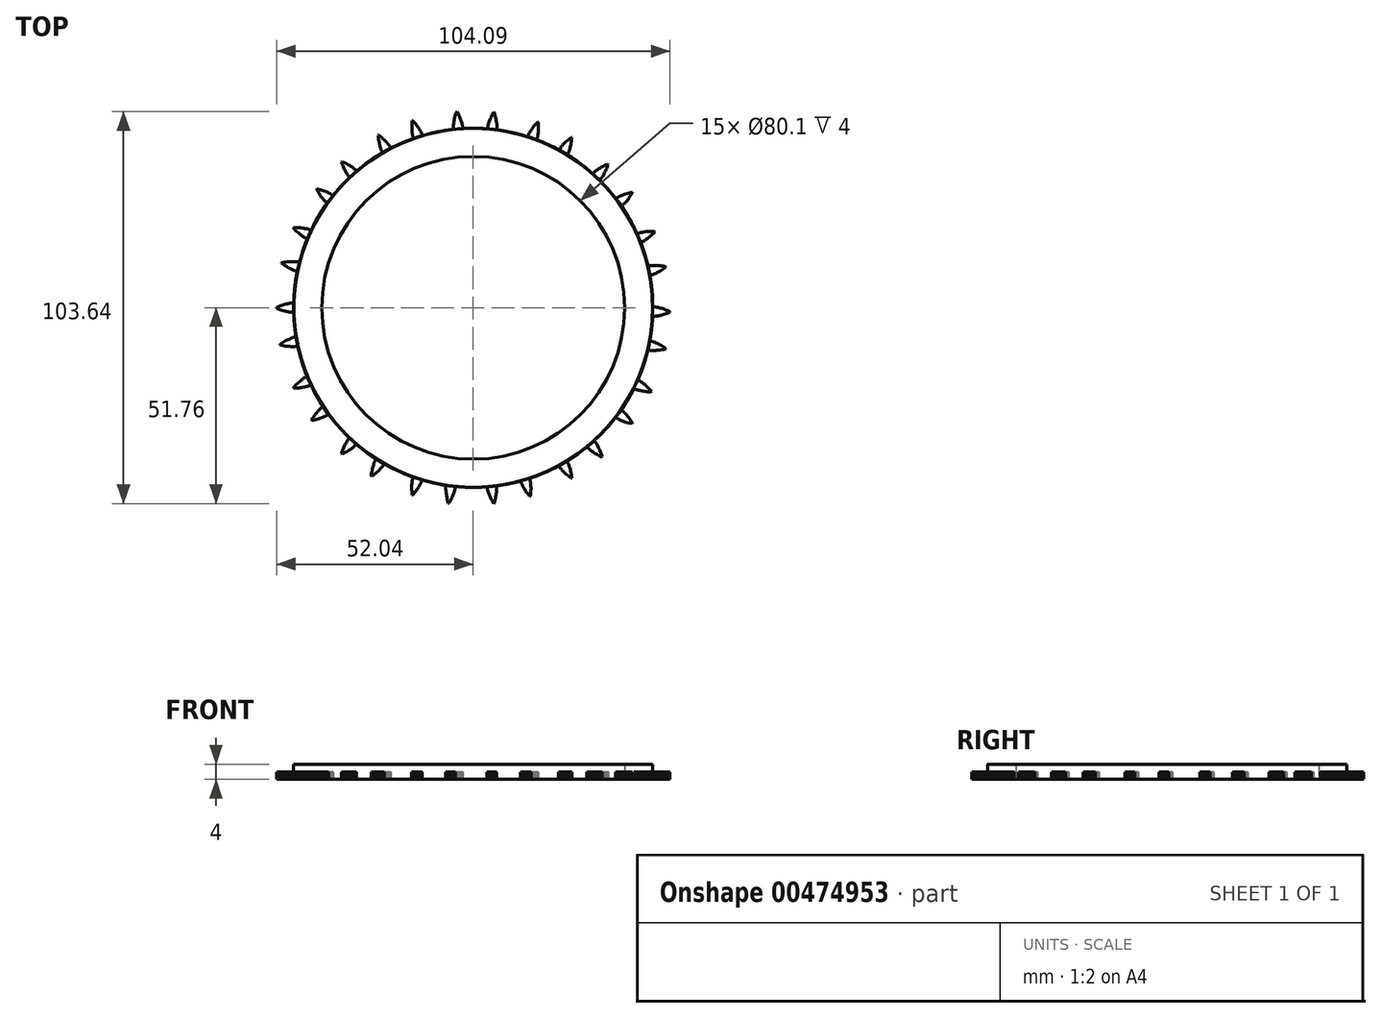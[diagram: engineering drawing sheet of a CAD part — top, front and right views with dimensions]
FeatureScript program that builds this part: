
annotation { "Feature Type Name" : "Feature", "Feature Type Description" : "" }
export const myFeature = defineFeature(function(context is Context, id is Id, definition is map)
    precondition{}
    {
        {
            var Q0;
            Q0=qCreatedBy(makeId("Top.planeOp"),FACE);
            var sketch = newSketch(context, id + "F0", { "sketchPlane" : qUnion([Q0])});
            skLineSegment(sketch, "E0", {"start": v(-4.56, -46.57) * mm, "end": v(-4.74, -47.51) * mm});
            skLineSegment(sketch, "E1", {"start": v(-4.74, -47.51) * mm, "end": v(-4.74, -47.52) * mm});
            skLineSegment(sketch, "E2", {"start": v(-4.74, -47.52) * mm, "end": v(-4.75, -47.57) * mm});
            skLineSegment(sketch, "E3", {"start": v(-4.75, -47.57) * mm, "end": v(-4.76, -47.64) * mm});
            skLineSegment(sketch, "E4", {"start": v(-4.76, -47.64) * mm, "end": v(-4.78, -47.75) * mm});
            skLineSegment(sketch, "E5", {"start": v(-4.78, -47.75) * mm, "end": v(-4.81, -47.89) * mm});
            skLineSegment(sketch, "E6", {"start": v(-4.81, -47.89) * mm, "end": v(-4.85, -48.05) * mm});
            skLineSegment(sketch, "E7", {"start": v(-4.85, -48.05) * mm, "end": v(-4.9, -48.25) * mm});
            skLineSegment(sketch, "E8", {"start": v(-4.9, -48.25) * mm, "end": v(-4.97, -48.47) * mm});
            skLineSegment(sketch, "E9", {"start": v(-4.97, -48.47) * mm, "end": v(-5.06, -48.72) * mm});
            skLineSegment(sketch, "E10", {"start": v(-5.06, -48.72) * mm, "end": v(-5.15, -49) * mm});
            skLineSegment(sketch, "E11", {"start": v(-5.15, -49) * mm, "end": v(-5.27, -49.31) * mm});
            skLineSegment(sketch, "E12", {"start": v(-5.27, -49.31) * mm, "end": v(-5.41, -49.64) * mm});
            skLineSegment(sketch, "E13", {"start": v(-5.41, -49.64) * mm, "end": v(-5.57, -50) * mm});
            skLineSegment(sketch, "E14", {"start": v(-5.57, -50) * mm, "end": v(-5.75, -50.38) * mm});
            skLineSegment(sketch, "E15", {"start": v(-5.75, -50.38) * mm, "end": v(-5.96, -50.79) * mm});
            skLineSegment(sketch, "E16", {"start": v(-5.96, -50.79) * mm, "end": v(-6.19, -51.21) * mm});
            skLineSegment(sketch, "E17", {"start": v(-6.19, -51.21) * mm, "end": v(-6.44, -51.66) * mm});
            skLineSegment(sketch, "E18", {"start": v(-6.6, -51.64) * mm, "end": v(-6.74, -51.14) * mm});
            skLineSegment(sketch, "E19", {"start": v(-6.74, -51.14) * mm, "end": v(-6.86, -50.67) * mm});
            skLineSegment(sketch, "E20", {"start": v(-6.86, -50.67) * mm, "end": v(-6.96, -50.23) * mm});
            skLineSegment(sketch, "E21", {"start": v(-6.96, -50.23) * mm, "end": v(-7.04, -49.81) * mm});
            skLineSegment(sketch, "E22", {"start": v(-7.04, -49.81) * mm, "end": v(-7.1, -49.43) * mm});
            skLineSegment(sketch, "E23", {"start": v(-7.1, -49.43) * mm, "end": v(-7.16, -49.07) * mm});
            skLineSegment(sketch, "E24", {"start": v(-7.16, -49.07) * mm, "end": v(-7.2, -48.75) * mm});
            skLineSegment(sketch, "E25", {"start": v(-7.2, -48.75) * mm, "end": v(-7.22, -48.45) * mm});
            skLineSegment(sketch, "E26", {"start": v(-7.22, -48.45) * mm, "end": v(-7.24, -48.19) * mm});
            skLineSegment(sketch, "E27", {"start": v(-7.24, -48.19) * mm, "end": v(-7.25, -47.95) * mm});
            skLineSegment(sketch, "E28", {"start": v(-7.25, -47.95) * mm, "end": v(-7.25, -47.75) * mm});
            skLineSegment(sketch, "E29", {"start": v(-7.25, -47.75) * mm, "end": v(-7.25, -47.58) * mm});
            skLineSegment(sketch, "E30", {"start": v(-7.25, -47.58) * mm, "end": v(-7.24, -47.44) * mm});
            skLineSegment(sketch, "E31", {"start": v(-7.24, -47.44) * mm, "end": v(-7.24, -47.33) * mm});
            skLineSegment(sketch, "E32", {"start": v(-7.24, -47.33) * mm, "end": v(-7.23, -47.26) * mm});
            skLineSegment(sketch, "E33", {"start": v(-7.23, -47.26) * mm, "end": v(-7.22, -47.21) * mm});
            skLineSegment(sketch, "E34", {"start": v(-7.22, -47.21) * mm, "end": v(-7.22, -47.2) * mm});
            skLineSegment(sketch, "E35", {"start": v(-7.22, -47.2) * mm, "end": v(-7.16, -46.24) * mm});
            skCircle(sketch, "E36", {"center": v(0, 0) * mm, "radius": 4 * mm});
            skCircle(sketch, "E37", {"center": v(0, 0) * mm, "radius": 46.8 * mm});
            skLineSegment(sketch, "E38", {"start": v(0, 0) * mm, "end": v(-16.38, -55.1) * mm, "construction": true});
            skLineSegment(sketch, "E39", {"start": v(-6.6, -51.64) * mm, "end": v(-6.44, -51.66) * mm});
            skCircle(sketch, "E40", {"center": v(0, 0) * mm, "radius": 40.05 * mm});
            skLineSegment(sketch, "E41", {"start": v(-13.27, -44.83) * mm, "end": v(-13.6, -45.73) * mm});
            skLineSegment(sketch, "E42", {"start": v(-13.6, -45.73) * mm, "end": v(-13.6, -45.74) * mm});
            skLineSegment(sketch, "E43", {"start": v(-13.6, -45.74) * mm, "end": v(-13.62, -45.78) * mm});
            skLineSegment(sketch, "E44", {"start": v(-13.62, -45.78) * mm, "end": v(-13.65, -45.86) * mm});
            skLineSegment(sketch, "E45", {"start": v(-13.65, -45.86) * mm, "end": v(-13.68, -45.96) * mm});
            skLineSegment(sketch, "E46", {"start": v(-13.68, -45.96) * mm, "end": v(-13.74, -46.09) * mm});
            skLineSegment(sketch, "E47", {"start": v(-13.74, -46.09) * mm, "end": v(-13.8, -46.24) * mm});
            skLineSegment(sketch, "E48", {"start": v(-13.8, -46.24) * mm, "end": v(-13.9, -46.43) * mm});
            skLineSegment(sketch, "E49", {"start": v(-13.9, -46.43) * mm, "end": v(-14, -46.63) * mm});
            skLineSegment(sketch, "E50", {"start": v(-14, -46.63) * mm, "end": v(-14.12, -46.87) * mm});
            skLineSegment(sketch, "E51", {"start": v(-14.12, -46.87) * mm, "end": v(-14.27, -47.13) * mm});
            skLineSegment(sketch, "E52", {"start": v(-14.27, -47.13) * mm, "end": v(-14.44, -47.4) * mm});
            skLineSegment(sketch, "E53", {"start": v(-14.44, -47.4) * mm, "end": v(-14.63, -47.71) * mm});
            skLineSegment(sketch, "E54", {"start": v(-14.63, -47.71) * mm, "end": v(-14.85, -48.03) * mm});
            skLineSegment(sketch, "E55", {"start": v(-14.85, -48.03) * mm, "end": v(-15.1, -48.38) * mm});
            skLineSegment(sketch, "E56", {"start": v(-15.1, -48.38) * mm, "end": v(-15.37, -48.74) * mm});
            skLineSegment(sketch, "E57", {"start": v(-15.37, -48.74) * mm, "end": v(-15.67, -49.12) * mm});
            skLineSegment(sketch, "E58", {"start": v(-15.67, -49.12) * mm, "end": v(-16, -49.52) * mm});
            skLineSegment(sketch, "E59", {"start": v(-16, -49.52) * mm, "end": v(-16.15, -49.47) * mm});
            skLineSegment(sketch, "E60", {"start": v(-16.15, -49.47) * mm, "end": v(-16.2, -48.96) * mm});
            skLineSegment(sketch, "E61", {"start": v(-16.2, -48.96) * mm, "end": v(-16.24, -48.47) * mm});
            skLineSegment(sketch, "E62", {"start": v(-16.24, -48.47) * mm, "end": v(-16.26, -48.02) * mm});
            skLineSegment(sketch, "E63", {"start": v(-16.26, -48.02) * mm, "end": v(-16.27, -47.6) * mm});
            skLineSegment(sketch, "E64", {"start": v(-16.27, -47.6) * mm, "end": v(-16.26, -47.2) * mm});
            skLineSegment(sketch, "E65", {"start": v(-16.26, -47.2) * mm, "end": v(-16.25, -46.85) * mm});
            skLineSegment(sketch, "E66", {"start": v(-16.25, -46.85) * mm, "end": v(-16.23, -46.52) * mm});
            skLineSegment(sketch, "E67", {"start": v(-16.23, -46.52) * mm, "end": v(-16.2, -46.22) * mm});
            skLineSegment(sketch, "E68", {"start": v(-16.2, -46.22) * mm, "end": v(-16.18, -45.96) * mm});
            skLineSegment(sketch, "E69", {"start": v(-16.18, -45.96) * mm, "end": v(-16.15, -45.73) * mm});
            skLineSegment(sketch, "E70", {"start": v(-16.15, -45.73) * mm, "end": v(-16.11, -45.53) * mm});
            skLineSegment(sketch, "E71", {"start": v(-16.11, -45.53) * mm, "end": v(-16.08, -45.36) * mm});
            skLineSegment(sketch, "E72", {"start": v(-16.08, -45.36) * mm, "end": v(-16.05, -45.22) * mm});
            skLineSegment(sketch, "E73", {"start": v(-16.05, -45.22) * mm, "end": v(-16.03, -45.12) * mm});
            skLineSegment(sketch, "E74", {"start": v(-16.03, -45.12) * mm, "end": v(-16, -45.04) * mm});
            skLineSegment(sketch, "E75", {"start": v(-16, -45.04) * mm, "end": v(-16, -45) * mm});
            skLineSegment(sketch, "E76", {"start": v(-16, -45) * mm, "end": v(-16, -44.99) * mm});
            skLineSegment(sketch, "E77", {"start": v(-16, -44.99) * mm, "end": v(-15.76, -44.06) * mm});
            skCircle(sketch, "E78", {"center": v(0, 0) * mm, "radius": 47.5 * mm});
            skSolve(sketch);
        }
        {
            var Q0;
            Q0=makeQuery(id+"F0.imprint","IMPRINT",FACE,{"disambiguationData":[TD([[makeQuery(id+"F0.imprint","IMPRINT",EDGE,{"derivedFrom":sQuery(id+"F0.wireOp",EDGE,"E40")}),-1.0]])]});
            var Q1;
            {var subQ0=sQuery(id+"F0.wireOp",EDGE,"E37");var subQ1=sQuery(id+"F0.wireOp",EDGE,"E0");var subQ2=makeQuery(id+"F0.imprint","INTERSECT",VERTEX,{"derivedFrom":[subQ1,subQ0]});Q1=makeQuery(id+"F0.imprint","IMPRINT",FACE,{"disambiguationData":[TD([[makeQuery(id+"F0.imprint","IMPRINT",EDGE,{"disambiguationData":[TD([[subQ2,-1.0]])],"derivedFrom":subQ1}),1.0]])]});}
            var Q2;
            {var subQ0=sQuery(id+"F0.wireOp",EDGE,"E37");var subQ1=sQuery(id+"F0.wireOp",EDGE,"E0");var subQ2=makeQuery(id+"F0.imprint","INTERSECT",VERTEX,{"derivedFrom":[subQ1,subQ0]});Q2=makeQuery(id+"F0.imprint","IMPRINT",FACE,{"disambiguationData":[TD([[makeQuery(id+"F0.imprint","IMPRINT",EDGE,{"disambiguationData":[TD([[subQ2,-1.0]])],"derivedFrom":subQ1}),-1.0]])]});}
            var Q3;
            {var subQ0=sQuery(id+"F0.wireOp",EDGE,"E37");var subQ1=sQuery(id+"F0.wireOp",EDGE,"E35");var subQ2=makeQuery(id+"F0.imprint","INTERSECT",VERTEX,{"derivedFrom":[subQ1,subQ0]});Q3=makeQuery(id+"F0.imprint","IMPRINT",FACE,{"disambiguationData":[TD([[makeQuery(id+"F0.imprint","IMPRINT",EDGE,{"disambiguationData":[TD([[subQ2,1.0]])],"derivedFrom":subQ1}),1.0]])]});}
            var Q4;
            {var subQ0=sQuery(id+"F0.wireOp",EDGE,"E77");var subQ1=sQuery(id+"F0.wireOp",EDGE,"E37");var subQ2=makeQuery(id+"F0.imprint","INTERSECT",VERTEX,{"derivedFrom":[subQ1,subQ0]});Q4=makeQuery(id+"F0.imprint","IMPRINT",FACE,{"disambiguationData":[TD([[makeQuery(id+"F0.imprint","IMPRINT",EDGE,{"disambiguationData":[TD([[subQ2,-1.0]])],"derivedFrom":subQ1}),-1.0]])]});}
            extrude(context, id + "F1", {"entities" : qUnion([Q0, Q1, Q2, Q3, Q4]), "depth" : 4 * mm});
        }
        {
            var Q0;
            {var subQ0=sQuery(id+"F0.wireOp",EDGE,"E0");Q0=makeQuery(id+"F0.imprint","IMPRINT",FACE,{"disambiguationData":[TD([[makeQuery(id+"F0.imprint","IMPRINT",EDGE,{"derivedFrom":subQ0}),-1.0]])]});}
            var Q1;
            {var subQ0=sQuery(id+"F0.wireOp",EDGE,"E42");Q1=makeQuery(id+"F0.imprint","IMPRINT",FACE,{"disambiguationData":[TD([[makeQuery(id+"F0.imprint","IMPRINT",EDGE,{"derivedFrom":subQ0}),-1.0]])]});}
            var Q2;
            {var subQ0=sQuery(id+"F0.wireOp",EDGE,"E1");Q2=makeQuery(id+"F0.imprint","IMPRINT",FACE,{"disambiguationData":[TD([[makeQuery(id+"F0.imprint","IMPRINT",EDGE,{"derivedFrom":subQ0}),-1.0]])]});}
            extrude(context, id + "F2", {"entities" : qUnion([Q0, Q1, Q2]), "operationType" : NewBodyOperationType.ADD, "depth" : 2 * mm});
        }
        {
            var Q0;
            Q0=makeQuery(id+"F1.opExtrude","SWEPT_BODY",BODY,{"disambiguationData":[OSD([sQuery(id+"F0.wireOp",EDGE,"E40"),sQuery(id+"F0.wireOp",EDGE,"E78")])]});
            var Q1;
            Q1=sQuery(id+"F0.wireOp",EDGE,"E78");
            circularPattern(context, id + "F3", {"entities" : qUnion([Q0]), "axis" : qUnion([Q1]), "angle" : 360 * degree, "instanceCount" : 15, "equalSpace" : true});
        }
    });
